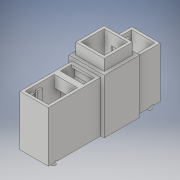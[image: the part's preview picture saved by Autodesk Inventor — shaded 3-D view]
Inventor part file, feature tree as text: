
AUTODESK INVENTOR PART (.ipt)
format: ipt  version: 2019 (Build 230136000, 136)  size: 512,512 bytes
history: native  units: mm
features: extrude x16, other x16, chamfer x2
ambient origin geometry x8: Origin, YZ Plane, XZ Plane, XY Plane, X Axis, Y Axis, Z Axis, Center Point
bodies: Solid1 (feature_tree)
feature tree (34):
  extrude  "BasePlate"  Depth=16.5mm
  extrude  "Separations"  Depth=65.0mm
  extrude  "Aperture1"  Depth=4.5mm
  extrude  "Aperture2"  Depth=2.7mm
  extrude  "Aperture3"  Depth=4.5mm
  extrude  "ApertureRef"  Depth=3.0mm TaperAngle=0.0deg
  chamfer  "ApertureRefChamfer"  Distance=3.5mm
  extrude  "Overlap"  Depth=3.5mm
  extrude  "SampleProtectionCutout"  Depth=14.0mm
  extrude  "ModuleSliders"  Depth=18.0mm
  extrude  "BaseplateComponentsCutout"  Depth=26.5mm
  extrude  "OuterWalls"  Depth=2.0mm
  extrude  "ExpansionHeaderCutout"  TaperAngle=135.0deg  [1 undecoded]
  extrude  "AlignmentPads"  Depth=3.5mm
  extrude  "SampleGuideSpacer"  Depth=13.5mm
  extrude  "SampleGuide"  Depth=10.0mm
  chamfer  "RefSensorChamfer"  Angle=135.0deg  [1 undecoded]
  extrude  "AlignmentPadsRecess"  Depth=11.7mm
  other  "BasePlateSketch"
  other  "SeparationsSketch"
  other  "Aperture1Sketch"
  other  "Aperture2Sketch"
  other  "Aperture3Sketch"
  other  "ApertureRefSketch"
  other  "OverlapSketch"
  other  "SampleProtectionCutoutSketch"
  other  "ModuleSlidersSketch"
  other  "BaseplateComponentsCutoutSketch"
  other  "OuterWallsSketch"
  other  "ExpansionHeaderCutoutSketch"
  other  "AlignmentPadsSketch"
  other  "SampleGuideSpacerSketch"
  other  "SampleGuideSketch"
  other  "AlignmentPadsRecessSketch"
note: 2 required parameter values undecoded (feature->parameter linkage not recoverable at this tier; creation-order binding heuristic only, values carry confidence <= 0.55)
